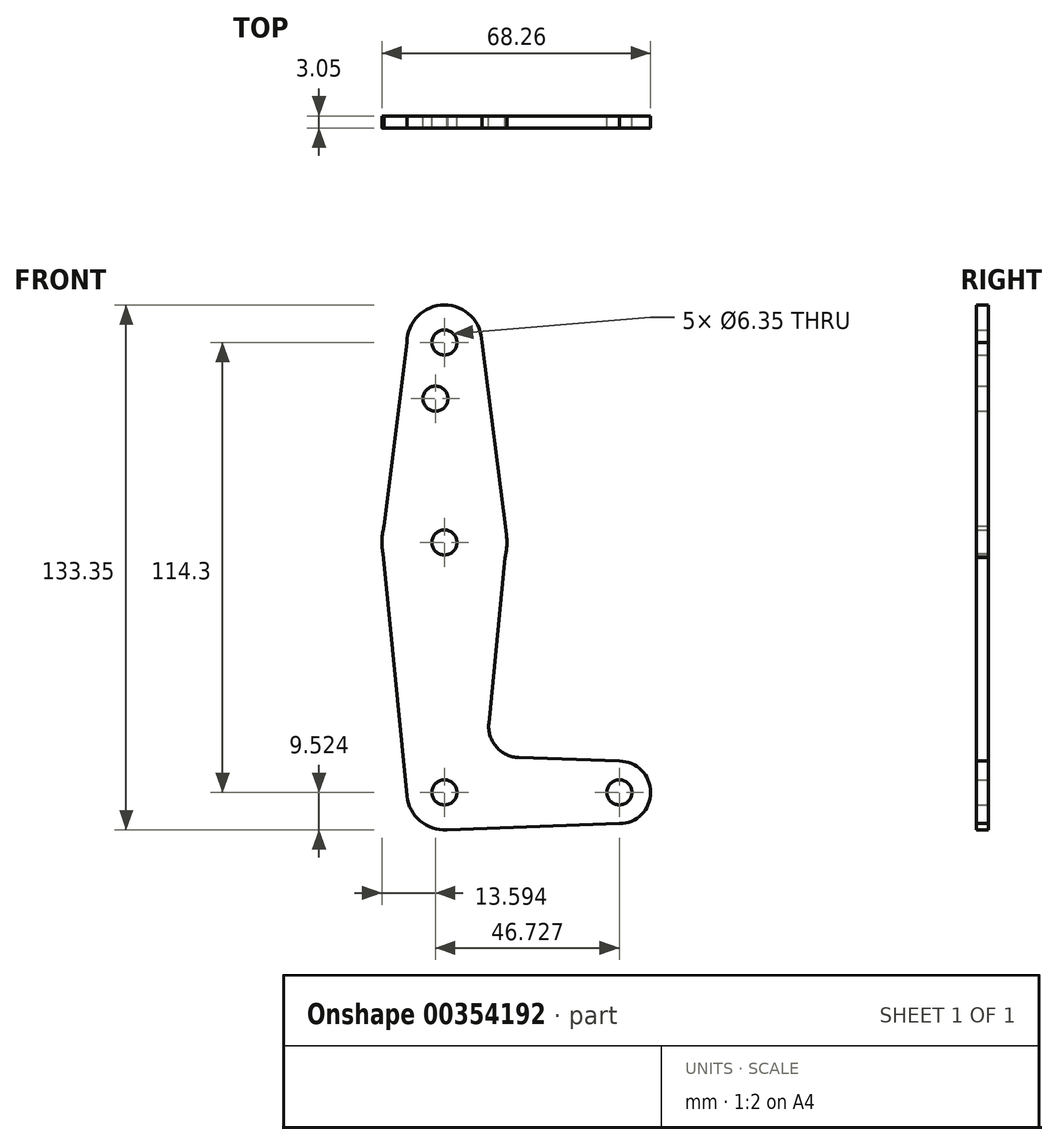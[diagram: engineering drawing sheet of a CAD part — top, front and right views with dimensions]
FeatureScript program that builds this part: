
annotation { "Feature Type Name" : "Feature", "Feature Type Description" : "" }
export const myFeature = defineFeature(function(context is Context, id is Id, definition is map)
    precondition{}
    {
        {
            var Q0;
            Q0=qCreatedBy(makeId("Front.planeOp"),FACE);
            var sketch = newSketch(context, id + "F0", { "sketchPlane" : qUnion([Q0])});
            skLineSegment(sketch, "E0", {"start": v(-158.12, 120.4) * mm, "end": v(-158.12, 6.1) * mm});
            skLineSegment(sketch, "E1", {"start": v(-158.12, 6.1) * mm, "end": v(-113.67, 6.1) * mm});
            skCircle(sketch, "E2", {"center": v(-158.12, 120.4) * mm, "radius": 9.53 * mm});
            skCircle(sketch, "E3", {"center": v(-158.12, 6.1) * mm, "radius": 9.53 * mm});
            skCircle(sketch, "E4", {"center": v(-113.67, 6.1) * mm, "radius": 7.94 * mm});
            skCircle(sketch, "E5", {"center": v(-158.12, 69.6) * mm, "radius": 15.88 * mm});
            skLineSegment(sketch, "E6", {"start": v(-148.6, 120.4) * mm, "end": v(-142.37, 71.6) * mm});
            skLineSegment(sketch, "E7", {"start": v(-167.64, 120.4) * mm, "end": v(-173.99, 69.23) * mm});
            skLineSegment(sketch, "E8", {"start": v(-173.99, 69.23) * mm, "end": v(-167.6, 5.15) * mm});
            skLineSegment(sketch, "E9", {"start": v(-142.37, 69.23) * mm, "end": v(-146.83, 23.66) * mm});
            skLineSegment(sketch, "E10", {"start": v(-139.2, 14.94) * mm, "end": v(-113.67, 14.03) * mm});
            skCircle(sketch, "E11", {"center": v(-158.12, 120.4) * mm, "radius": 3.18 * mm});
            skCircle(sketch, "E12", {"center": v(-158.12, 69.6) * mm, "radius": 3.18 * mm});
            skCircle(sketch, "E13", {"center": v(-158.12, 6.1) * mm, "radius": 3.18 * mm});
            skCircle(sketch, "E14", {"center": v(-113.67, 6.1) * mm, "radius": 3.18 * mm});
            skCircle(sketch, "E15", {"center": v(-160.4, 106.12) * mm, "radius": 3.18 * mm});
            skPoint(sketch, "E16.newPointA", {"position": v(-148.64, 5.15) * mm});
            skArc(sketch, "E16.filletArc", {"start": v(-146.83, 23.66) * mm, "mid": v(-144.9, 17.65) * mm, "end": v(-139.2, 14.94) * mm});
            skLineSegment(sketch, "E17", {"start": v(-158.07, -3.43) * mm, "end": v(-113.67, -1.84) * mm});
            skSolve(sketch);
        }
        {
            var Q0;
            Q0 = qSketchRegion(id + "F0", true);
            var Q1;
            {var subQ0=sQuery(id+"F0.wireOp",EDGE,"E3");var subQ1=sQuery(id+"F0.wireOp",EDGE,"E0");var subQ2=makeQuery(id+"F0.imprint","INTERSECT",VERTEX,{"derivedFrom":[subQ1,subQ0]});Q1=makeQuery(id+"F0.imprint","IMPRINT",FACE,{"disambiguationData":[TD([[makeQuery(id+"F0.imprint","IMPRINT",EDGE,{"disambiguationData":[TD([[subQ2,-1.0]])],"derivedFrom":subQ1}),1.0]])]});}
            extrude(context, id + "F1", {"entities" : qUnion([Q0, Q1]), "depth" : 3.05 * mm});
        }
    });
